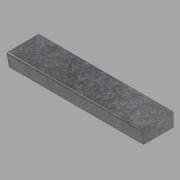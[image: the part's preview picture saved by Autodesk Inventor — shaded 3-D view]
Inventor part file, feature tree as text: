
AUTODESK INVENTOR PART (.ipt)
format: ipt  version: 2022.1 (Build 261234020, 234B)  size: 98,816 bytes
history: native  units: in
note: dims shown in document units (in); Inventor stores cm internally (conversion verified against a paired STEP export)
features: other x3, extrude x1, sketch x1
ambient origin geometry x8: Origin, YZ Plane, XZ Plane, XY Plane, X Axis, Y Axis, Z Axis, Center Point
bodies: Solid1 (feature_tree)
feature tree (5):
  other  "Blocks"
  extrude  "Extrusion1"  Depth=59.1875in TaperAngle=0.0deg
  sketch  "Sketch1"  dims[d0=13.0in d1=6.0in d2=13.5in d3=0.5in d4=0.5in d5=59.1875in d6=0.0in]
  other  "Profile"
  other  "Profile:1"
